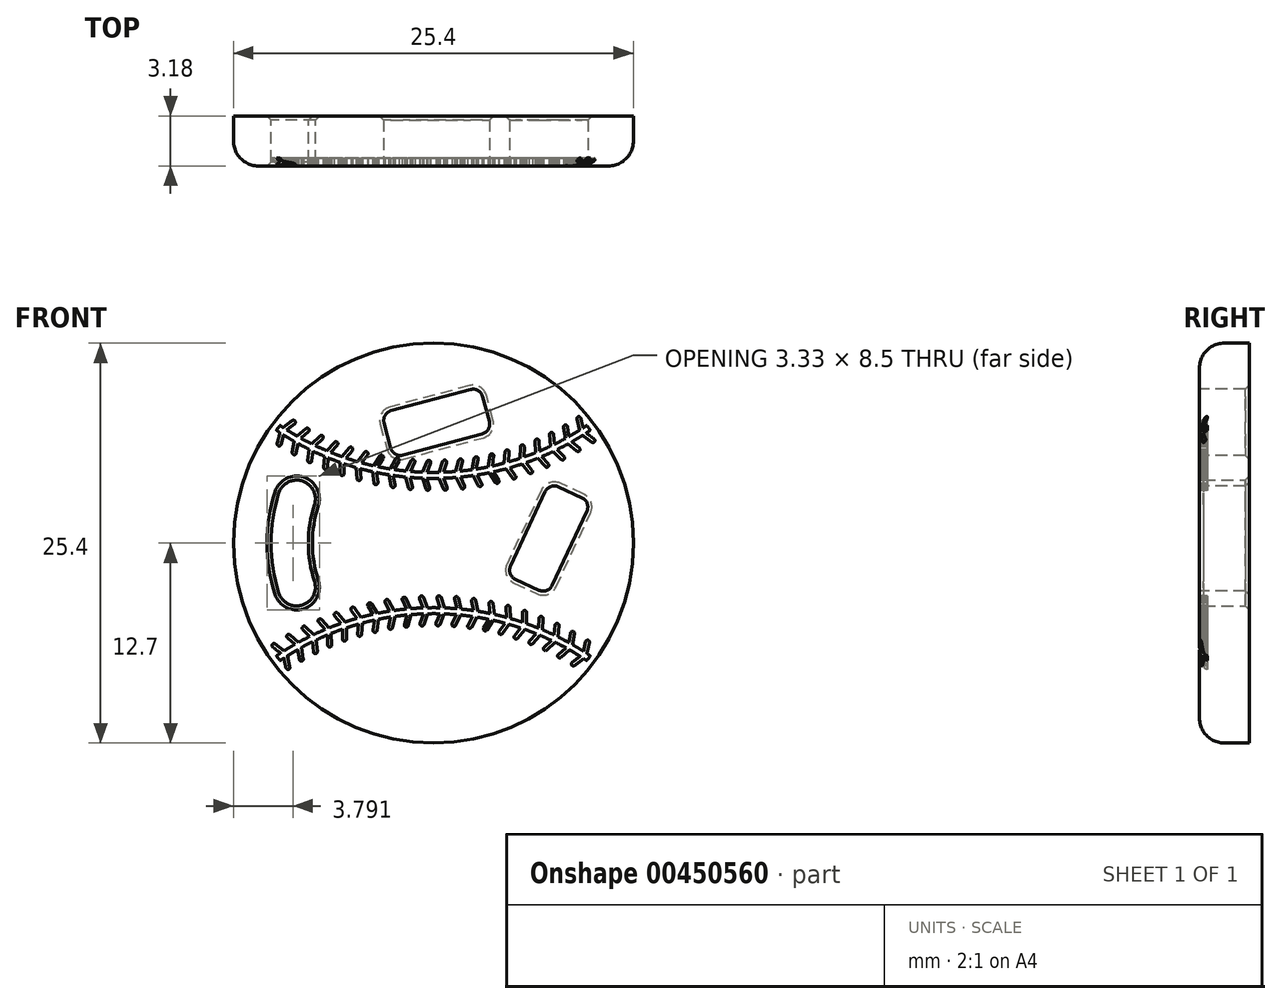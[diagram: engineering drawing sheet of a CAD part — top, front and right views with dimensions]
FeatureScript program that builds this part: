
annotation { "Feature Type Name" : "Feature", "Feature Type Description" : "" }
export const myFeature = defineFeature(function(context is Context, id is Id, definition is map)
    precondition{}
    {
        {
            var Q0;
            Q0=qCreatedBy(makeId("Front.planeOp"),FACE);
            var sketch = newSketch(context, id + "F0", { "sketchPlane" : qUnion([Q0])});
            skCircle(sketch, "E0", {"center": v(0, 0) * mm, "radius": 12.7 * mm});
            skArc(sketch, "E1", {"start": v(-9.82, 3.17) * mm, "mid": v(-10.32, 0) * mm, "end": v(-9.82, -3.17) * mm});
            skArc(sketch, "E2", {"start": v(-7.55, 2.44) * mm, "mid": v(-7.94, 0) * mm, "end": v(-7.55, -2.44) * mm});
            skArc(sketch, "E3", {"start": v(-7.55, 2.44) * mm, "mid": v(-8.32, 3.94) * mm, "end": v(-9.82, 3.18) * mm});
            skArc(sketch, "E4", {"start": v(-9.82, -3.18) * mm, "mid": v(-8.32, -3.94) * mm, "end": v(-7.55, -2.44) * mm});
            skLineSegment(sketch, "E5", {"start": v(-7.55, 0) * mm, "end": v(-7.55, -2.44) * mm, "construction": true});
            skPoint(sketch, "E6", {"position": v(-7.55, 0) * mm});
            skLineSegment(sketch, "E7", {"start": v(-7.55, 2.44) * mm, "end": v(-7.55, 0) * mm, "construction": true});
            skLineSegment(sketch, "E8", {"start": v(-7.55, 0) * mm, "end": v(0, 0) * mm, "construction": true});
            skSolve(sketch);
        }
        {
            var Q0;
            Q0 = qSketchRegion(id + "F0", true);
            extrude(context, id + "F1", {"entities" : qUnion([Q0]), "depth" : 3.17 * mm});
        }
        {
            var Q0;
            Q0=makeQuery(id+"F1.opExtrude","CAP_EDGE",EDGE,{"disambiguationData":[OSD([sQuery(id+"F0.wireOp",EDGE,"E4")])],"isStart":false});
            var Q1;
            Q1=makeQuery(id+"F1.opExtrude","CAP_EDGE",EDGE,{"disambiguationData":[OSD([sQuery(id+"F0.wireOp",EDGE,"E2")])],"isStart":false});
            var Q2;
            Q2=makeQuery(id+"F1.opExtrude","CAP_EDGE",EDGE,{"disambiguationData":[OSD([sQuery(id+"F0.wireOp",EDGE,"E2")])],"isStart":true});
            chamfer(context, id + "F2", {"entities" : qUnion([Q0, Q1, Q2]), "width" : 0.25 * mm, "tangentPropagation" : true});
        }
        {
            var Q0;
            Q0=makeQuery(id+"F1.opExtrude","CAP_FACE",FACE,{"disambiguationData":[OSD([sQuery(id+"F0.wireOp",EDGE,"E0"),sQuery(id+"F0.wireOp",EDGE,"E1"),sQuery(id+"F0.wireOp",EDGE,"E2"),sQuery(id+"F0.wireOp",EDGE,"E3"),sQuery(id+"F0.wireOp",EDGE,"E4")])],"isStart":false});
            var sketch = newSketch(context, id + "F3", { "sketchPlane" : qUnion([Q0])});
            skLineSegment(sketch, "E9.bottom", {"start": v(0, -3.18) * mm, "end": v(-19.05, -3.18) * mm, "construction": true});
            skLineSegment(sketch, "E9.top", {"start": v(0, 3.18) * mm, "end": v(-19.05, 3.17) * mm, "construction": true});
            skLineSegment(sketch, "E9.left", {"start": v(0, -3.18) * mm, "end": v(0, 3.18) * mm, "construction": true});
            skLineSegment(sketch, "E9.right", {"start": v(-19.05, -3.18) * mm, "end": v(-19.05, 3.17) * mm, "construction": true});
            skSolve(sketch);
        }
        {
            var Q0;
            {var subQ4=sQuery(id+"F0.wireOp",EDGE,"E0");Q0=makeQuery(id+"F3.imprint","IMPRINT",FACE,{"disambiguationData":[TD([[makeQuery(id+"F3.imprint","IMPRINT",EDGE,{"derivedFrom":makeQuery(id+"F1.opExtrude","CAP_EDGE",EDGE,{"disambiguationData":[OSD([subQ4])],"isStart":false})}),1.0]])]});}
            var sketch = newSketch(context, id + "F4", { "sketchPlane" : qUnion([Q0])});
            skCircle(sketch, "E10", {"center": v(0, 0) * mm, "radius": 12.7 * mm, "construction": true});
            skArc(sketch, "E11", {"start": v(-10.1, 7.71) * mm, "mid": v(0, 4.49) * mm, "end": v(10.1, 7.71) * mm});
            skArc(sketch, "E12", {"start": v(-10.32, 7.4) * mm, "mid": v(0, 4.1) * mm, "end": v(10.32, 7.4) * mm});
            skLineSegment(sketch, "E13", {"start": v(0, 12.7) * mm, "end": v(0, 8.6) * mm, "construction": true});
            skLineSegment(sketch, "E14", {"start": v(0, 8.6) * mm, "end": v(0, 4.49) * mm, "construction": true});
            skLineSegment(sketch, "E15", {"start": v(0, 4.1) * mm, "end": v(0, 0) * mm, "construction": true});
            skArc(sketch, "E16", {"start": v(-10.1, 7.71) * mm, "mid": v(-10.2, 7.56) * mm, "end": v(-10.32, 7.4) * mm});
            skArc(sketch, "E17", {"start": v(10.32, 7.4) * mm, "mid": v(10.2, 7.56) * mm, "end": v(10.1, 7.71) * mm});
            skArc(sketch, "E18.MirrorCS", {"start": v(-10.1, -7.71) * mm, "mid": v(0, -4.49) * mm, "end": v(10.1, -7.71) * mm});
            skArc(sketch, "E19.MirrorCS", {"start": v(-10.32, -7.4) * mm, "mid": v(0, -4.1) * mm, "end": v(10.32, -7.4) * mm});
            skArc(sketch, "E20.MirrorCS", {"start": v(10.32, -7.4) * mm, "mid": v(10.2, -7.56) * mm, "end": v(10.1, -7.71) * mm});
            skArc(sketch, "E21.MirrorCS", {"start": v(-10.1, -7.71) * mm, "mid": v(-10.2, -7.56) * mm, "end": v(-10.32, -7.4) * mm});
            skSolve(sketch);
        }
        {
            var Q0;
            Q0 = qSketchRegion(id + "F4", true);
            extrude(context, id + "F5", {"entities" : qUnion([Q0]), "operationType" : NewBodyOperationType.REMOVE, "oppositeDirection" : true, "depth" : 0.5 * mm});
        }
        {
            var Q0;
            {var subQ4=sQuery(id+"F0.wireOp",EDGE,"E0");Q0=makeQuery(id+"F3.imprint","IMPRINT",FACE,{"disambiguationData":[TD([[makeQuery(id+"F3.imprint","IMPRINT",EDGE,{"derivedFrom":makeQuery(id+"F1.opExtrude","CAP_EDGE",EDGE,{"disambiguationData":[OSD([subQ4])],"isStart":false})}),1.0]])]});}
            var sketch = newSketch(context, id + "F6", { "sketchPlane" : qUnion([Q0])});
            skCircle(sketch, "E22", {"center": v(0, 0) * mm, "radius": 12.7 * mm, "construction": true});
            skArc(sketch, "E23", {"start": v(10.32, -7.4) * mm, "mid": v(0, -4.1) * mm, "end": v(-10.32, -7.4) * mm, "construction": true});
            skArc(sketch, "E24", {"start": v(10.1, -7.71) * mm, "mid": v(0, -4.49) * mm, "end": v(-10.1, -7.71) * mm, "construction": true});
            skLineSegment(sketch, "E25", {"start": v(0, 0) * mm, "end": v(0, -4.1) * mm, "construction": true});
            skLineSegment(sketch, "E26", {"start": v(0, -4.49) * mm, "end": v(0, -8.6) * mm, "construction": true});
            skPoint(sketch, "E26.endSnap0", {"position": v(0, -4.49) * mm});
            skLineSegment(sketch, "E27", {"start": v(0, -8.6) * mm, "end": v(0, -12.7) * mm, "construction": true});
            skArc(sketch, "E28", {"start": v(-10.32, -7.4) * mm, "mid": v(-10.2, -7.56) * mm, "end": v(-10.1, -7.71) * mm, "construction": true});
            skArc(sketch, "E29", {"start": v(10.1, -7.71) * mm, "mid": v(10.2, -7.56) * mm, "end": v(10.32, -7.4) * mm, "construction": true});
            skArc(sketch, "E30", {"start": v(10.2, -7.56) * mm, "mid": v(0, -4.3) * mm, "end": v(-10.2, -7.56) * mm});
            skLineSegment(sketch, "E31", {"start": v(0, -4.1) * mm, "end": v(0, -4.3) * mm, "construction": true});
            skLineSegment(sketch, "E32", {"start": v(0, -4.3) * mm, "end": v(0, -4.49) * mm, "construction": true});
            skLineSegment(sketch, "E33", {"start": v(-9.79, -7.27) * mm, "end": v(-9.37, -7.93) * mm, "construction": true});
            skLineSegment(sketch, "E34", {"start": v(-10.2, -6.6) * mm, "end": v(-9.55, -7.11) * mm});
            skLineSegment(sketch, "E35", {"start": v(-9.55, -7.11) * mm, "end": v(-9.37, -7.93) * mm});
            skArc(sketch, "E36", {"start": v(-10.05, -6.4) * mm, "mid": v(-10.23, -6.43) * mm, "end": v(-10.2, -6.6) * mm});
            skLineSegment(sketch, "E37", {"start": v(-10.05, -6.4) * mm, "end": v(-9.32, -6.97) * mm});
            skLineSegment(sketch, "E38", {"start": v(-9.32, -6.97) * mm, "end": v(-9.12, -7.88) * mm});
            skArc(sketch, "E39", {"start": v(-9.37, -7.93) * mm, "mid": v(-9.22, -8.03) * mm, "end": v(-9.12, -7.88) * mm});
            skLineSegment(sketch, "E40", {"start": v(-10.2, -6.6) * mm, "end": v(-9.79, -7.27) * mm, "construction": true});
            skLineSegment(sketch, "E41.1.0", {"start": v(-9.27, -6.02) * mm, "end": v(-8.64, -6.57) * mm});
            skLineSegment(sketch, "E41.1.1", {"start": v(-8.64, -6.57) * mm, "end": v(-8.51, -7.4) * mm});
            skArc(sketch, "E41.1.2", {"start": v(-8.51, -7.4) * mm, "mid": v(-8.37, -7.5) * mm, "end": v(-8.26, -7.35) * mm});
            skLineSegment(sketch, "E41.1.3", {"start": v(-8.4, -6.44) * mm, "end": v(-8.26, -7.35) * mm});
            skLineSegment(sketch, "E41.1.4", {"start": v(-9.1, -5.83) * mm, "end": v(-8.4, -6.44) * mm});
            skArc(sketch, "E41.1.5", {"start": v(-9.1, -5.83) * mm, "mid": v(-9.28, -5.84) * mm, "end": v(-9.27, -6.02) * mm});
            skLineSegment(sketch, "E41.2.0", {"start": v(-8.3, -5.5) * mm, "end": v(-7.7, -6.07) * mm});
            skLineSegment(sketch, "E41.2.1", {"start": v(-7.7, -6.07) * mm, "end": v(-7.63, -6.9) * mm});
            skArc(sketch, "E41.2.2", {"start": v(-7.63, -6.9) * mm, "mid": v(-7.49, -7.02) * mm, "end": v(-7.37, -6.88) * mm});
            skLineSegment(sketch, "E41.2.3", {"start": v(-7.46, -5.96) * mm, "end": v(-7.37, -6.88) * mm});
            skLineSegment(sketch, "E41.2.4", {"start": v(-8.12, -5.31) * mm, "end": v(-7.46, -5.96) * mm});
            skArc(sketch, "E41.2.5", {"start": v(-8.12, -5.31) * mm, "mid": v(-8.3, -5.32) * mm, "end": v(-8.3, -5.5) * mm});
            skLineSegment(sketch, "E41.3.0", {"start": v(-7.3, -5.03) * mm, "end": v(-6.74, -5.64) * mm});
            skLineSegment(sketch, "E41.3.1", {"start": v(-6.74, -5.64) * mm, "end": v(-6.71, -6.48) * mm});
            skArc(sketch, "E41.3.2", {"start": v(-6.71, -6.48) * mm, "mid": v(-6.58, -6.6) * mm, "end": v(-6.46, -6.47) * mm});
            skLineSegment(sketch, "E41.3.3", {"start": v(-6.5, -5.54) * mm, "end": v(-6.46, -6.47) * mm});
            skLineSegment(sketch, "E41.3.4", {"start": v(-7.1, -4.86) * mm, "end": v(-6.5, -5.54) * mm});
            skArc(sketch, "E41.3.5", {"start": v(-7.1, -4.86) * mm, "mid": v(-7.29, -4.85) * mm, "end": v(-7.3, -5.03) * mm});
            skLineSegment(sketch, "E41.4.0", {"start": v(-6.27, -4.62) * mm, "end": v(-5.75, -5.26) * mm});
            skLineSegment(sketch, "E41.4.1", {"start": v(-5.75, -5.26) * mm, "end": v(-5.77, -6.1) * mm});
            skArc(sketch, "E41.4.2", {"start": v(-5.77, -6.1) * mm, "mid": v(-5.65, -6.23) * mm, "end": v(-5.52, -6.1) * mm});
            skLineSegment(sketch, "E41.4.3", {"start": v(-5.5, -5.18) * mm, "end": v(-5.52, -6.1) * mm});
            skLineSegment(sketch, "E41.4.4", {"start": v(-6.07, -4.46) * mm, "end": v(-5.5, -5.18) * mm});
            skArc(sketch, "E41.4.5", {"start": v(-6.07, -4.46) * mm, "mid": v(-6.25, -4.44) * mm, "end": v(-6.27, -4.62) * mm});
            skLineSegment(sketch, "E41.5.0", {"start": v(-5.22, -4.27) * mm, "end": v(-4.74, -4.95) * mm});
            skLineSegment(sketch, "E41.5.1", {"start": v(-4.74, -4.95) * mm, "end": v(-4.81, -5.78) * mm});
            skArc(sketch, "E41.5.2", {"start": v(-4.81, -5.78) * mm, "mid": v(-4.7, -5.92) * mm, "end": v(-4.56, -5.8) * mm});
            skLineSegment(sketch, "E41.5.3", {"start": v(-4.48, -4.88) * mm, "end": v(-4.56, -5.8) * mm});
            skLineSegment(sketch, "E41.5.4", {"start": v(-5.01, -4.13) * mm, "end": v(-4.48, -4.88) * mm});
            skArc(sketch, "E41.5.5", {"start": v(-5.01, -4.13) * mm, "mid": v(-5.19, -4.1) * mm, "end": v(-5.22, -4.27) * mm});
            skLineSegment(sketch, "E41.6.0", {"start": v(-4.15, -4) * mm, "end": v(-3.72, -4.7) * mm});
            skLineSegment(sketch, "E41.6.1", {"start": v(-3.72, -4.7) * mm, "end": v(-3.84, -5.52) * mm});
            skArc(sketch, "E41.6.2", {"start": v(-3.84, -5.52) * mm, "mid": v(-3.73, -5.67) * mm, "end": v(-3.58, -5.56) * mm});
            skLineSegment(sketch, "E41.6.3", {"start": v(-3.45, -4.64) * mm, "end": v(-3.58, -5.56) * mm});
            skLineSegment(sketch, "E41.6.4", {"start": v(-3.94, -3.86) * mm, "end": v(-3.45, -4.64) * mm});
            skArc(sketch, "E41.6.5", {"start": v(-3.94, -3.86) * mm, "mid": v(-4.11, -3.82) * mm, "end": v(-4.15, -4) * mm});
            skLineSegment(sketch, "E41.7.0", {"start": v(-3.07, -3.77) * mm, "end": v(-2.68, -4.5) * mm});
            skLineSegment(sketch, "E41.7.1", {"start": v(-2.68, -4.5) * mm, "end": v(-2.84, -5.32) * mm});
            skArc(sketch, "E41.7.2", {"start": v(-2.84, -5.32) * mm, "mid": v(-2.75, -5.47) * mm, "end": v(-2.6, -5.37) * mm});
            skLineSegment(sketch, "E41.7.3", {"start": v(-2.4, -4.46) * mm, "end": v(-2.6, -5.37) * mm});
            skLineSegment(sketch, "E41.7.4", {"start": v(-2.84, -3.65) * mm, "end": v(-2.4, -4.46) * mm});
            skArc(sketch, "E41.7.5", {"start": v(-2.84, -3.65) * mm, "mid": v(-3.02, -3.6) * mm, "end": v(-3.07, -3.77) * mm});
            skLineSegment(sketch, "E41.8.0", {"start": v(-1.97, -3.62) * mm, "end": v(-1.62, -4.37) * mm});
            skLineSegment(sketch, "E41.8.1", {"start": v(-1.62, -4.37) * mm, "end": v(-1.84, -5.18) * mm});
            skArc(sketch, "E41.8.2", {"start": v(-1.84, -5.18) * mm, "mid": v(-1.75, -5.34) * mm, "end": v(-1.6, -5.25) * mm});
            skLineSegment(sketch, "E41.8.3", {"start": v(-1.36, -4.35) * mm, "end": v(-1.6, -5.25) * mm});
            skLineSegment(sketch, "E41.8.4", {"start": v(-1.74, -3.51) * mm, "end": v(-1.36, -4.35) * mm});
            skArc(sketch, "E41.8.5", {"start": v(-1.74, -3.51) * mm, "mid": v(-1.91, -3.45) * mm, "end": v(-1.97, -3.62) * mm});
            skLineSegment(sketch, "E41.9.0", {"start": v(-0.87, -3.54) * mm, "end": v(-0.57, -4.3) * mm});
            skLineSegment(sketch, "E41.9.1", {"start": v(-0.57, -4.3) * mm, "end": v(-0.84, -5.1) * mm});
            skArc(sketch, "E41.9.2", {"start": v(-0.84, -5.1) * mm, "mid": v(-0.76, -5.26) * mm, "end": v(-0.6, -5.18) * mm});
            skLineSegment(sketch, "E41.9.3", {"start": v(-0.3, -4.3) * mm, "end": v(-0.6, -5.18) * mm});
            skLineSegment(sketch, "E41.9.4", {"start": v(-0.63, -3.44) * mm, "end": v(-0.3, -4.3) * mm});
            skArc(sketch, "E41.9.5", {"start": v(-0.63, -3.44) * mm, "mid": v(-0.8, -3.37) * mm, "end": v(-0.87, -3.54) * mm});
            skLineSegment(sketch, "E41.10.0", {"start": v(0.23, -3.52) * mm, "end": v(0.49, -4.3) * mm});
            skLineSegment(sketch, "E41.10.1", {"start": v(0.49, -4.3) * mm, "end": v(0.18, -5.08) * mm});
            skArc(sketch, "E41.10.2", {"start": v(0.18, -5.08) * mm, "mid": v(0.25, -5.24) * mm, "end": v(0.41, -5.17) * mm});
            skLineSegment(sketch, "E41.10.3", {"start": v(0.76, -4.31) * mm, "end": v(0.41, -5.17) * mm});
            skLineSegment(sketch, "E41.10.4", {"start": v(0.48, -3.44) * mm, "end": v(0.76, -4.31) * mm});
            skArc(sketch, "E41.10.5", {"start": v(0.48, -3.44) * mm, "mid": v(0.32, -3.36) * mm, "end": v(0.23, -3.52) * mm});
            skLineSegment(sketch, "E41.11.0", {"start": v(1.34, -3.56) * mm, "end": v(1.55, -4.36) * mm});
            skLineSegment(sketch, "E41.11.1", {"start": v(1.55, -4.36) * mm, "end": v(1.19, -5.12) * mm});
            skArc(sketch, "E41.11.2", {"start": v(1.19, -5.12) * mm, "mid": v(1.25, -5.29) * mm, "end": v(1.41, -5.23) * mm});
            skLineSegment(sketch, "E41.11.3", {"start": v(1.81, -4.4) * mm, "end": v(1.41, -5.23) * mm});
            skLineSegment(sketch, "E41.11.4", {"start": v(1.58, -3.5) * mm, "end": v(1.81, -4.4) * mm});
            skArc(sketch, "E41.11.5", {"start": v(1.58, -3.5) * mm, "mid": v(1.43, -3.4) * mm, "end": v(1.34, -3.56) * mm});
            skLineSegment(sketch, "E41.12.0", {"start": v(2.44, -3.68) * mm, "end": v(2.6, -4.49) * mm});
            skLineSegment(sketch, "E41.12.1", {"start": v(2.6, -4.49) * mm, "end": v(2.2, -5.22) * mm});
            skArc(sketch, "E41.12.2", {"start": v(2.2, -5.22) * mm, "mid": v(2.24, -5.4) * mm, "end": v(2.41, -5.34) * mm});
            skLineSegment(sketch, "E41.12.3", {"start": v(2.86, -4.53) * mm, "end": v(2.41, -5.34) * mm});
            skLineSegment(sketch, "E41.12.4", {"start": v(2.69, -3.63) * mm, "end": v(2.86, -4.53) * mm});
            skArc(sketch, "E41.12.5", {"start": v(2.69, -3.63) * mm, "mid": v(2.54, -3.53) * mm, "end": v(2.44, -3.68) * mm});
            skLineSegment(sketch, "E41.13.0", {"start": v(3.53, -3.86) * mm, "end": v(3.64, -4.68) * mm});
            skLineSegment(sketch, "E41.13.1", {"start": v(3.64, -4.68) * mm, "end": v(3.19, -5.38) * mm});
            skArc(sketch, "E41.13.2", {"start": v(3.19, -5.38) * mm, "mid": v(3.23, -5.56) * mm, "end": v(3.4, -5.52) * mm});
            skLineSegment(sketch, "E41.13.3", {"start": v(3.9, -4.74) * mm, "end": v(3.4, -5.52) * mm});
            skLineSegment(sketch, "E41.13.4", {"start": v(3.78, -3.82) * mm, "end": v(3.9, -4.74) * mm});
            skArc(sketch, "E41.13.5", {"start": v(3.78, -3.82) * mm, "mid": v(3.64, -3.71) * mm, "end": v(3.53, -3.86) * mm});
            skLineSegment(sketch, "E41.14.0", {"start": v(4.6, -4.1) * mm, "end": v(4.67, -4.93) * mm});
            skLineSegment(sketch, "E41.14.1", {"start": v(4.67, -4.93) * mm, "end": v(4.18, -5.6) * mm});
            skArc(sketch, "E41.14.2", {"start": v(4.18, -5.6) * mm, "mid": v(4.2, -5.78) * mm, "end": v(4.38, -5.75) * mm});
            skLineSegment(sketch, "E41.14.3", {"start": v(4.93, -5) * mm, "end": v(4.38, -5.75) * mm});
            skLineSegment(sketch, "E41.14.4", {"start": v(4.86, -4.08) * mm, "end": v(4.93, -5) * mm});
            skArc(sketch, "E41.14.5", {"start": v(4.86, -4.08) * mm, "mid": v(4.72, -3.97) * mm, "end": v(4.6, -4.1) * mm});
            skLineSegment(sketch, "E41.15.0", {"start": v(5.67, -4.41) * mm, "end": v(5.68, -5.24) * mm});
            skLineSegment(sketch, "E41.15.1", {"start": v(5.68, -5.24) * mm, "end": v(5.15, -5.89) * mm});
            skArc(sketch, "E41.15.2", {"start": v(5.15, -5.89) * mm, "mid": v(5.17, -6.06) * mm, "end": v(5.34, -6.05) * mm});
            skLineSegment(sketch, "E41.15.3", {"start": v(5.93, -5.33) * mm, "end": v(5.34, -6.05) * mm});
            skLineSegment(sketch, "E41.15.4", {"start": v(5.92, -4.4) * mm, "end": v(5.93, -5.33) * mm});
            skArc(sketch, "E41.15.5", {"start": v(5.92, -4.4) * mm, "mid": v(5.8, -4.28) * mm, "end": v(5.67, -4.41) * mm});
            skLineSegment(sketch, "E41.16.0", {"start": v(6.7, -4.78) * mm, "end": v(6.67, -5.6) * mm});
            skLineSegment(sketch, "E41.16.1", {"start": v(6.67, -5.6) * mm, "end": v(6.1, -6.22) * mm});
            skArc(sketch, "E41.16.2", {"start": v(6.1, -6.22) * mm, "mid": v(6.1, -6.4) * mm, "end": v(6.29, -6.4) * mm});
            skLineSegment(sketch, "E41.16.3", {"start": v(6.92, -5.71) * mm, "end": v(6.29, -6.4) * mm});
            skLineSegment(sketch, "E41.16.4", {"start": v(6.96, -4.8) * mm, "end": v(6.92, -5.71) * mm});
            skArc(sketch, "E41.16.5", {"start": v(6.96, -4.8) * mm, "mid": v(6.84, -4.66) * mm, "end": v(6.7, -4.78) * mm});
            skLineSegment(sketch, "E41.17.0", {"start": v(7.72, -5.22) * mm, "end": v(7.63, -6.04) * mm});
            skLineSegment(sketch, "E41.17.1", {"start": v(7.63, -6.04) * mm, "end": v(7.03, -6.62) * mm});
            skArc(sketch, "E41.17.2", {"start": v(7.03, -6.62) * mm, "mid": v(7.03, -6.8) * mm, "end": v(7.2, -6.8) * mm});
            skLineSegment(sketch, "E41.17.3", {"start": v(7.88, -6.16) * mm, "end": v(7.2, -6.8) * mm});
            skLineSegment(sketch, "E41.17.4", {"start": v(7.98, -5.24) * mm, "end": v(7.88, -6.16) * mm});
            skArc(sketch, "E41.17.5", {"start": v(7.98, -5.24) * mm, "mid": v(7.86, -5.1) * mm, "end": v(7.72, -5.22) * mm});
            skLineSegment(sketch, "E41.18.0", {"start": v(8.71, -5.71) * mm, "end": v(8.57, -6.53) * mm});
            skLineSegment(sketch, "E41.18.1", {"start": v(8.57, -6.53) * mm, "end": v(7.94, -7.07) * mm});
            skArc(sketch, "E41.18.2", {"start": v(7.94, -7.07) * mm, "mid": v(7.92, -7.25) * mm, "end": v(8.1, -7.26) * mm});
            skLineSegment(sketch, "E41.18.3", {"start": v(8.8, -6.66) * mm, "end": v(8.1, -7.26) * mm});
            skLineSegment(sketch, "E41.18.4", {"start": v(8.96, -5.75) * mm, "end": v(8.8, -6.66) * mm});
            skArc(sketch, "E41.18.5", {"start": v(8.96, -5.75) * mm, "mid": v(8.86, -5.6) * mm, "end": v(8.71, -5.71) * mm});
            skLineSegment(sketch, "E41.19.0", {"start": v(9.67, -6.27) * mm, "end": v(9.48, -7.07) * mm});
            skLineSegment(sketch, "E41.19.1", {"start": v(9.48, -7.07) * mm, "end": v(8.81, -7.57) * mm});
            skArc(sketch, "E41.19.2", {"start": v(8.81, -7.57) * mm, "mid": v(8.79, -7.75) * mm, "end": v(8.97, -7.78) * mm});
            skLineSegment(sketch, "E41.19.3", {"start": v(9.7, -7.22) * mm, "end": v(8.97, -7.78) * mm});
            skLineSegment(sketch, "E41.19.4", {"start": v(9.92, -6.32) * mm, "end": v(9.7, -7.22) * mm});
            skArc(sketch, "E41.19.5", {"start": v(9.92, -6.32) * mm, "mid": v(9.82, -6.17) * mm, "end": v(9.67, -6.27) * mm});
            skLineSegment(sketch, "E41.anchor1", {"start": v(0, -21.89) * mm, "end": v(-10.2, -6.6) * mm, "construction": true});
            skLineSegment(sketch, "E41.anchor2", {"start": v(0, -21.89) * mm, "end": v(9.67, -6.27) * mm, "construction": true});
            skSolve(sketch);
        }
        {
            var Q0;
            Q0 = qSketchRegion(id + "F6", true);
            extrude(context, id + "F7", {"entities" : qUnion([Q0]), "operationType" : NewBodyOperationType.REMOVE, "oppositeDirection" : true, "depth" : 0.5 * mm});
        }
        {
            var Q0;
            {var subQ4=sQuery(id+"F0.wireOp",EDGE,"E0");Q0=makeQuery(id+"F3.imprint","IMPRINT",FACE,{"disambiguationData":[TD([[makeQuery(id+"F3.imprint","IMPRINT",EDGE,{"derivedFrom":makeQuery(id+"F1.opExtrude","CAP_EDGE",EDGE,{"disambiguationData":[OSD([subQ4])],"isStart":false})}),1.0]])]});}
            var sketch = newSketch(context, id + "F8", { "sketchPlane" : qUnion([Q0])});
            skCircle(sketch, "E42", {"center": v(0, 0) * mm, "radius": 12.7 * mm, "construction": true});
            skArc(sketch, "E43", {"start": v(-10.1, 7.71) * mm, "mid": v(0, 4.49) * mm, "end": v(10.1, 7.71) * mm, "construction": true});
            skArc(sketch, "E44", {"start": v(-10.32, 7.4) * mm, "mid": v(0, 4.1) * mm, "end": v(10.32, 7.4) * mm, "construction": true});
            skLineSegment(sketch, "E45", {"start": v(0, 12.7) * mm, "end": v(0, 8.6) * mm, "construction": true});
            skLineSegment(sketch, "E46", {"start": v(0, 8.6) * mm, "end": v(0, 4.49) * mm, "construction": true});
            skLineSegment(sketch, "E47", {"start": v(0, 4.1) * mm, "end": v(0, 0) * mm, "construction": true});
            skArc(sketch, "E48", {"start": v(-10.1, 7.71) * mm, "mid": v(-10.2, 7.56) * mm, "end": v(-10.32, 7.4) * mm, "construction": true});
            skArc(sketch, "E49", {"start": v(10.32, 7.4) * mm, "mid": v(10.2, 7.56) * mm, "end": v(10.1, 7.71) * mm, "construction": true});
            skArc(sketch, "E50", {"start": v(-10.2, 7.56) * mm, "mid": v(0, 4.3) * mm, "end": v(10.2, 7.56) * mm});
            skLineSegment(sketch, "E51", {"start": v(0, 4.49) * mm, "end": v(0, 4.3) * mm, "construction": true});
            skLineSegment(sketch, "E52", {"start": v(0, 4.3) * mm, "end": v(0, 4.1) * mm, "construction": true});
            skLineSegment(sketch, "E53", {"start": v(9.55, 7.11) * mm, "end": v(9.37, 7.93) * mm});
            skLineSegment(sketch, "E54", {"start": v(9.32, 6.97) * mm, "end": v(9.12, 7.88) * mm});
            skLineSegment(sketch, "E55", {"start": v(9.32, 6.97) * mm, "end": v(10.05, 6.4) * mm});
            skLineSegment(sketch, "E56", {"start": v(9.55, 7.11) * mm, "end": v(10.2, 6.6) * mm});
            skArc(sketch, "E57", {"start": v(9.37, 7.93) * mm, "mid": v(9.22, 8.03) * mm, "end": v(9.12, 7.88) * mm});
            skArc(sketch, "E58", {"start": v(10.05, 6.4) * mm, "mid": v(10.23, 6.43) * mm, "end": v(10.2, 6.6) * mm});
            skLineSegment(sketch, "E59", {"start": v(9.79, 7.27) * mm, "end": v(9.37, 7.93) * mm, "construction": true});
            skLineSegment(sketch, "E60", {"start": v(9.79, 7.27) * mm, "end": v(10.2, 6.6) * mm, "construction": true});
            skLineSegment(sketch, "E61.1.0", {"start": v(8.64, 6.57) * mm, "end": v(9.27, 6.02) * mm});
            skArc(sketch, "E61.1.1", {"start": v(9.1, 5.83) * mm, "mid": v(9.28, 5.84) * mm, "end": v(9.27, 6.02) * mm});
            skLineSegment(sketch, "E61.1.2", {"start": v(8.4, 6.44) * mm, "end": v(9.1, 5.83) * mm});
            skLineSegment(sketch, "E61.1.3", {"start": v(8.4, 6.44) * mm, "end": v(8.26, 7.35) * mm});
            skArc(sketch, "E61.1.4", {"start": v(8.51, 7.4) * mm, "mid": v(8.37, 7.5) * mm, "end": v(8.26, 7.35) * mm});
            skLineSegment(sketch, "E61.1.5", {"start": v(8.64, 6.57) * mm, "end": v(8.51, 7.4) * mm});
            skLineSegment(sketch, "E61.2.0", {"start": v(7.7, 6.07) * mm, "end": v(8.3, 5.5) * mm});
            skArc(sketch, "E61.2.1", {"start": v(8.12, 5.31) * mm, "mid": v(8.3, 5.32) * mm, "end": v(8.3, 5.5) * mm});
            skLineSegment(sketch, "E61.2.2", {"start": v(7.46, 5.96) * mm, "end": v(8.12, 5.31) * mm});
            skLineSegment(sketch, "E61.2.3", {"start": v(7.46, 5.96) * mm, "end": v(7.37, 6.88) * mm});
            skArc(sketch, "E61.2.4", {"start": v(7.63, 6.9) * mm, "mid": v(7.49, 7.02) * mm, "end": v(7.37, 6.88) * mm});
            skLineSegment(sketch, "E61.2.5", {"start": v(7.7, 6.07) * mm, "end": v(7.63, 6.9) * mm});
            skLineSegment(sketch, "E61.3.0", {"start": v(6.74, 5.64) * mm, "end": v(7.3, 5.03) * mm});
            skArc(sketch, "E61.3.1", {"start": v(7.1, 4.86) * mm, "mid": v(7.29, 4.85) * mm, "end": v(7.3, 5.03) * mm});
            skLineSegment(sketch, "E61.3.2", {"start": v(6.5, 5.54) * mm, "end": v(7.1, 4.86) * mm});
            skLineSegment(sketch, "E61.3.3", {"start": v(6.5, 5.54) * mm, "end": v(6.46, 6.47) * mm});
            skArc(sketch, "E61.3.4", {"start": v(6.71, 6.48) * mm, "mid": v(6.58, 6.6) * mm, "end": v(6.46, 6.47) * mm});
            skLineSegment(sketch, "E61.3.5", {"start": v(6.74, 5.64) * mm, "end": v(6.71, 6.48) * mm});
            skLineSegment(sketch, "E61.4.0", {"start": v(5.75, 5.26) * mm, "end": v(6.27, 4.62) * mm});
            skArc(sketch, "E61.4.1", {"start": v(6.07, 4.46) * mm, "mid": v(6.25, 4.44) * mm, "end": v(6.27, 4.62) * mm});
            skLineSegment(sketch, "E61.4.2", {"start": v(5.5, 5.18) * mm, "end": v(6.07, 4.46) * mm});
            skLineSegment(sketch, "E61.4.3", {"start": v(5.5, 5.18) * mm, "end": v(5.52, 6.1) * mm});
            skArc(sketch, "E61.4.4", {"start": v(5.77, 6.1) * mm, "mid": v(5.65, 6.23) * mm, "end": v(5.52, 6.1) * mm});
            skLineSegment(sketch, "E61.4.5", {"start": v(5.75, 5.26) * mm, "end": v(5.77, 6.1) * mm});
            skLineSegment(sketch, "E61.5.0", {"start": v(4.74, 4.95) * mm, "end": v(5.22, 4.27) * mm});
            skArc(sketch, "E61.5.1", {"start": v(5.01, 4.13) * mm, "mid": v(5.19, 4.1) * mm, "end": v(5.22, 4.27) * mm});
            skLineSegment(sketch, "E61.5.2", {"start": v(4.48, 4.88) * mm, "end": v(5.01, 4.13) * mm});
            skLineSegment(sketch, "E61.5.3", {"start": v(4.48, 4.88) * mm, "end": v(4.56, 5.8) * mm});
            skArc(sketch, "E61.5.4", {"start": v(4.81, 5.78) * mm, "mid": v(4.7, 5.92) * mm, "end": v(4.56, 5.8) * mm});
            skLineSegment(sketch, "E61.5.5", {"start": v(4.74, 4.95) * mm, "end": v(4.81, 5.78) * mm});
            skLineSegment(sketch, "E61.6.0", {"start": v(3.72, 4.7) * mm, "end": v(4.15, 4) * mm});
            skArc(sketch, "E61.6.1", {"start": v(3.94, 3.86) * mm, "mid": v(4.1, 3.82) * mm, "end": v(4.15, 4) * mm});
            skLineSegment(sketch, "E61.6.2", {"start": v(3.45, 4.64) * mm, "end": v(3.94, 3.86) * mm});
            skLineSegment(sketch, "E61.6.3", {"start": v(3.45, 4.64) * mm, "end": v(3.58, 5.56) * mm});
            skArc(sketch, "E61.6.4", {"start": v(3.84, 5.52) * mm, "mid": v(3.73, 5.67) * mm, "end": v(3.58, 5.56) * mm});
            skLineSegment(sketch, "E61.6.5", {"start": v(3.72, 4.7) * mm, "end": v(3.84, 5.52) * mm});
            skLineSegment(sketch, "E61.7.0", {"start": v(2.68, 4.5) * mm, "end": v(3.07, 3.77) * mm});
            skArc(sketch, "E61.7.1", {"start": v(2.84, 3.65) * mm, "mid": v(3.02, 3.6) * mm, "end": v(3.07, 3.77) * mm});
            skLineSegment(sketch, "E61.7.2", {"start": v(2.4, 4.46) * mm, "end": v(2.84, 3.65) * mm});
            skLineSegment(sketch, "E61.7.3", {"start": v(2.4, 4.46) * mm, "end": v(2.6, 5.37) * mm});
            skArc(sketch, "E61.7.4", {"start": v(2.84, 5.32) * mm, "mid": v(2.75, 5.47) * mm, "end": v(2.6, 5.37) * mm});
            skLineSegment(sketch, "E61.7.5", {"start": v(2.68, 4.5) * mm, "end": v(2.84, 5.32) * mm});
            skLineSegment(sketch, "E61.8.0", {"start": v(1.62, 4.37) * mm, "end": v(1.97, 3.62) * mm});
            skArc(sketch, "E61.8.1", {"start": v(1.74, 3.51) * mm, "mid": v(1.91, 3.45) * mm, "end": v(1.97, 3.62) * mm});
            skLineSegment(sketch, "E61.8.2", {"start": v(1.36, 4.35) * mm, "end": v(1.74, 3.51) * mm});
            skLineSegment(sketch, "E61.8.3", {"start": v(1.36, 4.35) * mm, "end": v(1.6, 5.25) * mm});
            skArc(sketch, "E61.8.4", {"start": v(1.84, 5.18) * mm, "mid": v(1.75, 5.34) * mm, "end": v(1.6, 5.25) * mm});
            skLineSegment(sketch, "E61.8.5", {"start": v(1.62, 4.37) * mm, "end": v(1.84, 5.18) * mm});
            skLineSegment(sketch, "E61.9.0", {"start": v(0.57, 4.3) * mm, "end": v(0.87, 3.54) * mm});
            skArc(sketch, "E61.9.1", {"start": v(0.63, 3.44) * mm, "mid": v(0.8, 3.37) * mm, "end": v(0.87, 3.54) * mm});
            skLineSegment(sketch, "E61.9.2", {"start": v(0.3, 4.3) * mm, "end": v(0.63, 3.44) * mm});
            skLineSegment(sketch, "E61.9.3", {"start": v(0.3, 4.3) * mm, "end": v(0.6, 5.18) * mm});
            skArc(sketch, "E61.9.4", {"start": v(0.84, 5.1) * mm, "mid": v(0.76, 5.26) * mm, "end": v(0.6, 5.18) * mm});
            skLineSegment(sketch, "E61.9.5", {"start": v(0.57, 4.3) * mm, "end": v(0.84, 5.1) * mm});
            skLineSegment(sketch, "E61.10.0", {"start": v(-0.49, 4.3) * mm, "end": v(-0.23, 3.52) * mm});
            skArc(sketch, "E61.10.1", {"start": v(-0.48, 3.44) * mm, "mid": v(-0.32, 3.36) * mm, "end": v(-0.23, 3.52) * mm});
            skLineSegment(sketch, "E61.10.2", {"start": v(-0.76, 4.31) * mm, "end": v(-0.48, 3.44) * mm});
            skLineSegment(sketch, "E61.10.3", {"start": v(-0.76, 4.31) * mm, "end": v(-0.41, 5.17) * mm});
            skArc(sketch, "E61.10.4", {"start": v(-0.18, 5.08) * mm, "mid": v(-0.25, 5.24) * mm, "end": v(-0.41, 5.17) * mm});
            skLineSegment(sketch, "E61.10.5", {"start": v(-0.49, 4.3) * mm, "end": v(-0.18, 5.08) * mm});
            skLineSegment(sketch, "E61.11.0", {"start": v(-1.55, 4.36) * mm, "end": v(-1.34, 3.56) * mm});
            skArc(sketch, "E61.11.1", {"start": v(-1.58, 3.5) * mm, "mid": v(-1.43, 3.4) * mm, "end": v(-1.34, 3.56) * mm});
            skLineSegment(sketch, "E61.11.2", {"start": v(-1.81, 4.4) * mm, "end": v(-1.58, 3.5) * mm});
            skLineSegment(sketch, "E61.11.3", {"start": v(-1.81, 4.4) * mm, "end": v(-1.41, 5.23) * mm});
            skArc(sketch, "E61.11.4", {"start": v(-1.19, 5.12) * mm, "mid": v(-1.25, 5.29) * mm, "end": v(-1.41, 5.23) * mm});
            skLineSegment(sketch, "E61.11.5", {"start": v(-1.55, 4.36) * mm, "end": v(-1.19, 5.12) * mm});
            skLineSegment(sketch, "E61.12.0", {"start": v(-2.6, 4.49) * mm, "end": v(-2.44, 3.68) * mm});
            skArc(sketch, "E61.12.1", {"start": v(-2.69, 3.63) * mm, "mid": v(-2.54, 3.53) * mm, "end": v(-2.44, 3.68) * mm});
            skLineSegment(sketch, "E61.12.2", {"start": v(-2.86, 4.53) * mm, "end": v(-2.69, 3.63) * mm});
            skLineSegment(sketch, "E61.12.3", {"start": v(-2.86, 4.53) * mm, "end": v(-2.41, 5.35) * mm});
            skArc(sketch, "E61.12.4", {"start": v(-2.2, 5.22) * mm, "mid": v(-2.24, 5.4) * mm, "end": v(-2.41, 5.35) * mm});
            skLineSegment(sketch, "E61.12.5", {"start": v(-2.6, 4.49) * mm, "end": v(-2.2, 5.22) * mm});
            skLineSegment(sketch, "E61.13.0", {"start": v(-3.64, 4.68) * mm, "end": v(-3.53, 3.86) * mm});
            skArc(sketch, "E61.13.1", {"start": v(-3.78, 3.82) * mm, "mid": v(-3.64, 3.71) * mm, "end": v(-3.53, 3.86) * mm});
            skLineSegment(sketch, "E61.13.2", {"start": v(-3.9, 4.74) * mm, "end": v(-3.78, 3.82) * mm});
            skLineSegment(sketch, "E61.13.3", {"start": v(-3.9, 4.74) * mm, "end": v(-3.4, 5.52) * mm});
            skArc(sketch, "E61.13.4", {"start": v(-3.19, 5.38) * mm, "mid": v(-3.23, 5.56) * mm, "end": v(-3.4, 5.52) * mm});
            skLineSegment(sketch, "E61.13.5", {"start": v(-3.64, 4.68) * mm, "end": v(-3.19, 5.38) * mm});
            skLineSegment(sketch, "E61.14.0", {"start": v(-4.67, 4.93) * mm, "end": v(-4.6, 4.1) * mm});
            skArc(sketch, "E61.14.1", {"start": v(-4.86, 4.08) * mm, "mid": v(-4.72, 3.97) * mm, "end": v(-4.6, 4.1) * mm});
            skLineSegment(sketch, "E61.14.2", {"start": v(-4.93, 5) * mm, "end": v(-4.86, 4.08) * mm});
            skLineSegment(sketch, "E61.14.3", {"start": v(-4.93, 5) * mm, "end": v(-4.38, 5.75) * mm});
            skArc(sketch, "E61.14.4", {"start": v(-4.18, 5.6) * mm, "mid": v(-4.2, 5.78) * mm, "end": v(-4.38, 5.75) * mm});
            skLineSegment(sketch, "E61.14.5", {"start": v(-4.67, 4.93) * mm, "end": v(-4.18, 5.6) * mm});
            skLineSegment(sketch, "E61.15.0", {"start": v(-5.68, 5.24) * mm, "end": v(-5.67, 4.41) * mm});
            skArc(sketch, "E61.15.1", {"start": v(-5.92, 4.4) * mm, "mid": v(-5.8, 4.28) * mm, "end": v(-5.67, 4.41) * mm});
            skLineSegment(sketch, "E61.15.2", {"start": v(-5.93, 5.33) * mm, "end": v(-5.92, 4.4) * mm});
            skLineSegment(sketch, "E61.15.3", {"start": v(-5.93, 5.33) * mm, "end": v(-5.34, 6.05) * mm});
            skArc(sketch, "E61.15.4", {"start": v(-5.15, 5.89) * mm, "mid": v(-5.17, 6.07) * mm, "end": v(-5.34, 6.05) * mm});
            skLineSegment(sketch, "E61.15.5", {"start": v(-5.68, 5.24) * mm, "end": v(-5.15, 5.89) * mm});
            skLineSegment(sketch, "E61.16.0", {"start": v(-6.67, 5.6) * mm, "end": v(-6.7, 4.78) * mm});
            skArc(sketch, "E61.16.1", {"start": v(-6.96, 4.8) * mm, "mid": v(-6.84, 4.66) * mm, "end": v(-6.7, 4.78) * mm});
            skLineSegment(sketch, "E61.16.2", {"start": v(-6.92, 5.71) * mm, "end": v(-6.96, 4.8) * mm});
            skLineSegment(sketch, "E61.16.3", {"start": v(-6.92, 5.71) * mm, "end": v(-6.29, 6.4) * mm});
            skArc(sketch, "E61.16.4", {"start": v(-6.1, 6.22) * mm, "mid": v(-6.1, 6.4) * mm, "end": v(-6.29, 6.4) * mm});
            skLineSegment(sketch, "E61.16.5", {"start": v(-6.67, 5.6) * mm, "end": v(-6.1, 6.22) * mm});
            skLineSegment(sketch, "E61.17.0", {"start": v(-7.63, 6.04) * mm, "end": v(-7.72, 5.22) * mm});
            skArc(sketch, "E61.17.1", {"start": v(-7.98, 5.24) * mm, "mid": v(-7.86, 5.1) * mm, "end": v(-7.72, 5.22) * mm});
            skLineSegment(sketch, "E61.17.2", {"start": v(-7.88, 6.16) * mm, "end": v(-7.98, 5.24) * mm});
            skLineSegment(sketch, "E61.17.3", {"start": v(-7.88, 6.16) * mm, "end": v(-7.2, 6.8) * mm});
            skArc(sketch, "E61.17.4", {"start": v(-7.03, 6.62) * mm, "mid": v(-7.03, 6.8) * mm, "end": v(-7.2, 6.8) * mm});
            skLineSegment(sketch, "E61.17.5", {"start": v(-7.63, 6.04) * mm, "end": v(-7.03, 6.62) * mm});
            skLineSegment(sketch, "E61.18.0", {"start": v(-8.57, 6.53) * mm, "end": v(-8.71, 5.71) * mm});
            skArc(sketch, "E61.18.1", {"start": v(-8.96, 5.75) * mm, "mid": v(-8.86, 5.6) * mm, "end": v(-8.71, 5.71) * mm});
            skLineSegment(sketch, "E61.18.2", {"start": v(-8.8, 6.66) * mm, "end": v(-8.96, 5.75) * mm});
            skLineSegment(sketch, "E61.18.3", {"start": v(-8.8, 6.66) * mm, "end": v(-8.1, 7.26) * mm});
            skArc(sketch, "E61.18.4", {"start": v(-7.94, 7.07) * mm, "mid": v(-7.92, 7.25) * mm, "end": v(-8.1, 7.26) * mm});
            skLineSegment(sketch, "E61.18.5", {"start": v(-8.57, 6.53) * mm, "end": v(-7.94, 7.07) * mm});
            skLineSegment(sketch, "E61.19.0", {"start": v(-9.48, 7.07) * mm, "end": v(-9.67, 6.27) * mm});
            skArc(sketch, "E61.19.1", {"start": v(-9.92, 6.32) * mm, "mid": v(-9.82, 6.17) * mm, "end": v(-9.67, 6.27) * mm});
            skLineSegment(sketch, "E61.19.2", {"start": v(-9.7, 7.22) * mm, "end": v(-9.92, 6.32) * mm});
            skLineSegment(sketch, "E61.19.3", {"start": v(-9.7, 7.22) * mm, "end": v(-8.97, 7.78) * mm});
            skArc(sketch, "E61.19.4", {"start": v(-8.81, 7.57) * mm, "mid": v(-8.79, 7.75) * mm, "end": v(-8.97, 7.78) * mm});
            skLineSegment(sketch, "E61.19.5", {"start": v(-9.48, 7.07) * mm, "end": v(-8.81, 7.57) * mm});
            skLineSegment(sketch, "E61.anchor1", {"start": v(0, 21.89) * mm, "end": v(9.55, 7.11) * mm, "construction": true});
            skLineSegment(sketch, "E61.anchor2", {"start": v(0, 21.89) * mm, "end": v(-9.48, 7.07) * mm, "construction": true});
            skSolve(sketch);
        }
        {
            var Q0;
            Q0 = qSketchRegion(id + "F8", true);
            extrude(context, id + "F9", {"entities" : qUnion([Q0]), "operationType" : NewBodyOperationType.REMOVE, "oppositeDirection" : true, "depth" : 0.5 * mm});
        }
        {
            var Q0;
            Q0=qCreatedBy(makeId("Top.planeOp"),FACE);
            var sketch = newSketch(context, id + "F10", { "sketchPlane" : qUnion([Q0])});
            skArc(sketch, "E62", {"start": v(-12.7, -1.59) * mm, "mid": v(-12.24, -2.71) * mm, "end": v(-11.11, -3.18) * mm});
            skLineSegment(sketch, "E63", {"start": v(-12.7, -1.59) * mm, "end": v(-12.7, -3.18) * mm});
            skLineSegment(sketch, "E64", {"start": v(-12.7, -3.18) * mm, "end": v(-11.11, -3.18) * mm});
            skSolve(sketch);
        }
        {
            var Q0;
            Q0=qCreatedBy(makeId("Top.planeOp"),FACE);
            var sketch = newSketch(context, id + "F11", { "sketchPlane" : qUnion([Q0])});
            skLineSegment(sketch, "E65", {"start": v(0, 0) * mm, "end": v(0, -3.18) * mm});
            skSolve(sketch);
        }
        {
            var Q0;
            Q0 = qSketchRegion(id + "F10", true);
            var Q1;
            Q1=sQuery(id+"F11.wireOp",EDGE,"E65");
            revolve(context, id + "F12", {"operationType" : NewBodyOperationType.REMOVE, "entities" : qUnion([Q0]), "axis" : qUnion([Q1]), "revolveType" : RevolveType.FULL, "oppositeDirection" : true});
        }
        {
            var Q0;
            {var subQ4=sQuery(id+"F0.wireOp",EDGE,"E0");Q0=makeQuery(id+"F3.imprint","IMPRINT",FACE,{"disambiguationData":[TD([[makeQuery(id+"F3.imprint","IMPRINT",EDGE,{"derivedFrom":makeQuery(id+"F1.opExtrude","CAP_EDGE",EDGE,{"disambiguationData":[OSD([subQ4])],"isStart":false})}),1.0]])]});}
            var sketch = newSketch(context, id + "F13", { "sketchPlane" : qUnion([Q0])});
            skLineSegment(sketch, "E66", {"start": v(7.1, 3.26) * mm, "end": v(4.9, -1.46) * mm});
            skLineSegment(sketch, "E67", {"start": v(5.2, -2.3) * mm, "end": v(6.7, -3) * mm});
            skLineSegment(sketch, "E68", {"start": v(7.55, -2.7) * mm, "end": v(9.75, 2.03) * mm});
            skLineSegment(sketch, "E69", {"start": v(9.44, 2.87) * mm, "end": v(7.95, 3.57) * mm});
            skPoint(sketch, "E70.visualSharp", {"position": v(7.37, 3.84) * mm});
            skArc(sketch, "E70.filletArc", {"start": v(7.95, 3.57) * mm, "mid": v(7.46, 3.6) * mm, "end": v(7.1, 3.26) * mm});
            skPoint(sketch, "E71.visualSharp", {"position": v(10.02, 2.6) * mm});
            skArc(sketch, "E71.filletArc", {"start": v(9.75, 2.03) * mm, "mid": v(9.77, 2.51) * mm, "end": v(9.44, 2.87) * mm});
            skPoint(sketch, "E72.visualSharp", {"position": v(7.28, -3.27) * mm});
            skArc(sketch, "E72.filletArc", {"start": v(6.7, -3) * mm, "mid": v(7.2, -3.02) * mm, "end": v(7.55, -2.7) * mm});
            skPoint(sketch, "E73.visualSharp", {"position": v(4.63, -2.03) * mm});
            skArc(sketch, "E73.filletArc", {"start": v(4.9, -1.46) * mm, "mid": v(4.88, -1.94) * mm, "end": v(5.2, -2.3) * mm});
            skSolve(sketch);
        }
        {
            var Q0;
            Q0 = qSketchRegion(id + "F13", true);
            extrude(context, id + "F14", {"entities" : qUnion([Q0]), "operationType" : NewBodyOperationType.REMOVE, "oppositeDirection" : true, "depth" : 25.4 * mm});
        }
        {
            var Q0;
            Q0=makeQuery(id+"F14.boolean.opBoolean","COPY",EDGE,{"derivedFrom":makeQuery(id+"F14.opExtrude","CAP_EDGE",EDGE,{"disambiguationData":[OSD([sQuery(id+"F13.wireOp",EDGE,"E66")])],"isStart":true})});
            var Q1;
            Q1=makeQuery(id+"F14.boolean.opBoolean","INTERSECT",EDGE,{"derivedFrom":[makeQuery(id+"F1.opExtrude","CAP_FACE",FACE,{"disambiguationData":[OSD([sQuery(id+"F0.wireOp",EDGE,"E0"),sQuery(id+"F0.wireOp",EDGE,"E1"),sQuery(id+"F0.wireOp",EDGE,"E2"),sQuery(id+"F0.wireOp",EDGE,"E3"),sQuery(id+"F0.wireOp",EDGE,"E4")])],"isStart":true}),makeQuery(id+"F14.opExtrude","SWEPT_FACE",FACE,{"disambiguationData":[OSD([sQuery(id+"F13.wireOp",EDGE,"E66")])]})]});
            chamfer(context, id + "F15", {"entities" : qUnion([Q0, Q1]), "width" : 0.25 * mm, "tangentPropagation" : true});
        }
        {
            var Q0;
            {var subQ4=sQuery(id+"F0.wireOp",EDGE,"E0");Q0=makeQuery(id+"F3.imprint","IMPRINT",FACE,{"disambiguationData":[TD([[makeQuery(id+"F3.imprint","IMPRINT",EDGE,{"derivedFrom":makeQuery(id+"F1.opExtrude","CAP_EDGE",EDGE,{"disambiguationData":[OSD([subQ4])],"isStart":false})}),1.0]])]});}
            var sketch = newSketch(context, id + "F16", { "sketchPlane" : qUnion([Q0])});
            skLineSegment(sketch, "E74", {"start": v(-2.68, 8.4) * mm, "end": v(2.35, 9.75) * mm});
            skLineSegment(sketch, "E75", {"start": v(3.12, 9.3) * mm, "end": v(3.55, 7.71) * mm});
            skLineSegment(sketch, "E76", {"start": v(3.1, 6.93) * mm, "end": v(-1.93, 5.58) * mm});
            skLineSegment(sketch, "E77", {"start": v(-2.7, 6.03) * mm, "end": v(-3.13, 7.63) * mm});
            skPoint(sketch, "E78.visualSharp", {"position": v(-3.3, 8.24) * mm});
            skArc(sketch, "E78.filletArc", {"start": v(-2.68, 8.4) * mm, "mid": v(-3.07, 8.11) * mm, "end": v(-3.13, 7.63) * mm});
            skPoint(sketch, "E79.visualSharp", {"position": v(2.96, 9.92) * mm});
            skArc(sketch, "E79.filletArc", {"start": v(3.12, 9.3) * mm, "mid": v(2.83, 9.7) * mm, "end": v(2.35, 9.75) * mm});
            skPoint(sketch, "E80.visualSharp", {"position": v(3.72, 7.1) * mm});
            skArc(sketch, "E80.filletArc", {"start": v(3.1, 6.93) * mm, "mid": v(3.49, 7.23) * mm, "end": v(3.55, 7.71) * mm});
            skPoint(sketch, "E81.visualSharp", {"position": v(-2.54, 5.42) * mm});
            skArc(sketch, "E81.filletArc", {"start": v(-2.7, 6.03) * mm, "mid": v(-2.4, 5.65) * mm, "end": v(-1.93, 5.58) * mm});
            skSolve(sketch);
        }
        {
            var Q0;
            Q0 = qSketchRegion(id + "F16", true);
            extrude(context, id + "F17", {"entities" : qUnion([Q0]), "operationType" : NewBodyOperationType.REMOVE, "oppositeDirection" : true, "depth" : 25.4 * mm});
        }
        {
            var Q0;
            Q0=makeQuery(id+"F17.boolean.opBoolean","COPY",EDGE,{"derivedFrom":makeQuery(id+"F17.opExtrude","CAP_EDGE",EDGE,{"disambiguationData":[OSD([sQuery(id+"F16.wireOp",EDGE,"E77")])],"isStart":true})});
            var Q1;
            Q1=makeQuery(id+"F17.boolean.opBoolean","INTERSECT",EDGE,{"derivedFrom":[makeQuery(id+"F1.opExtrude","CAP_FACE",FACE,{"disambiguationData":[OSD([sQuery(id+"F0.wireOp",EDGE,"E0"),sQuery(id+"F0.wireOp",EDGE,"E1"),sQuery(id+"F0.wireOp",EDGE,"E2"),sQuery(id+"F0.wireOp",EDGE,"E3"),sQuery(id+"F0.wireOp",EDGE,"E4")])],"isStart":true}),makeQuery(id+"F17.opExtrude","SWEPT_FACE",FACE,{"disambiguationData":[OSD([sQuery(id+"F16.wireOp",EDGE,"E76")])]})]});
            chamfer(context, id + "F18", {"entities" : qUnion([Q0, Q1]), "width" : 0.25 * mm, "tangentPropagation" : true});
        }
    });
